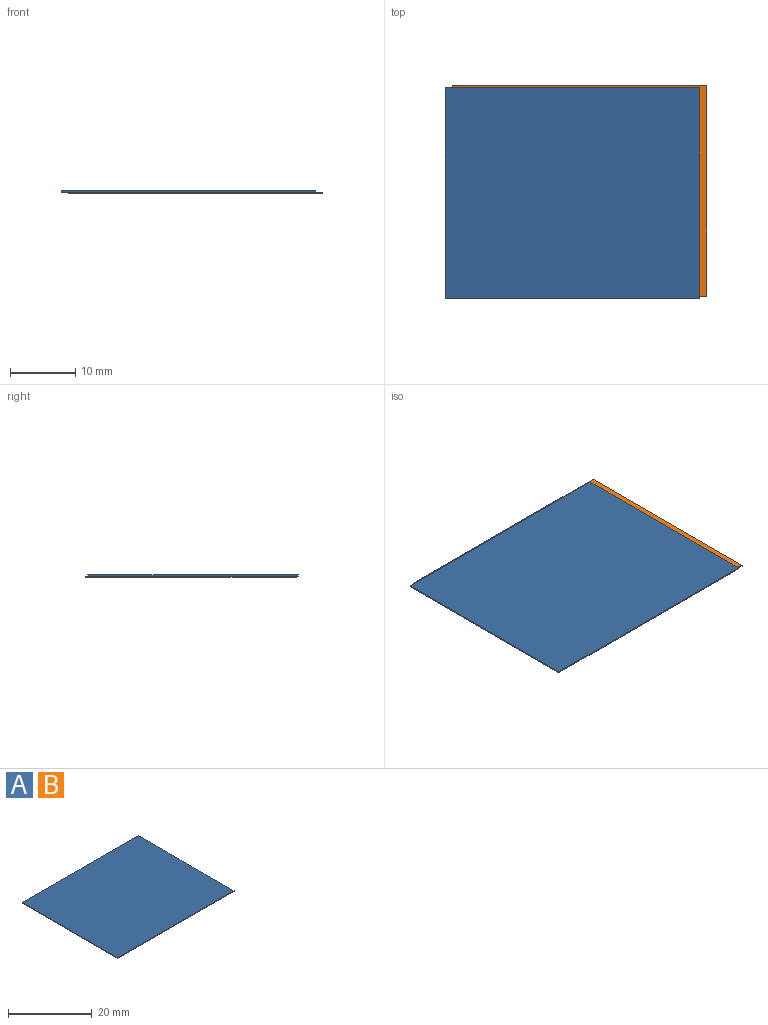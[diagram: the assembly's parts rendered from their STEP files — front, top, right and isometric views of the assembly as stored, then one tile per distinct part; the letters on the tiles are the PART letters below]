
ASSEMBLY  parts=2 mates=1
PART A: 6 faces, bbox 39.1x32.4x0.2 mm
  f0: plane 32.37x0.17mm, normal (-1,0,0), area 5.5mm2, adj f1,f3,f4,f5
  f1: plane 39.14x0.17mm, normal (0,-1,0), area 6.7mm2, adj f0,f2,f4,f5
  f2: plane 32.37x0.17mm, normal (1,0,0), area 5.5mm2, adj f1,f3,f4,f5
  f3: plane 39.14x0.17mm, normal (0,1,0), area 6.7mm2, adj f0,f2,f4,f5
  f4: plane 39.14x32.37mm, normal (0,0,1), area 1267.1mm2, adj f0,f1,f2,f3
  f5: plane 39.14x32.37mm, normal (0,0,-1), area 1267.1mm2, adj f0,f1,f2,f3
PART B: same geometry as A
PLACE A t=(-2.67,-6.15,-2.62)mm
PLACE B t=(-1.64,-5.82,-2.79)mm
MATE planar A.f5 <-> B.f4  axis (0,0,-1) through (16.9,10.03,-2.62)mm
